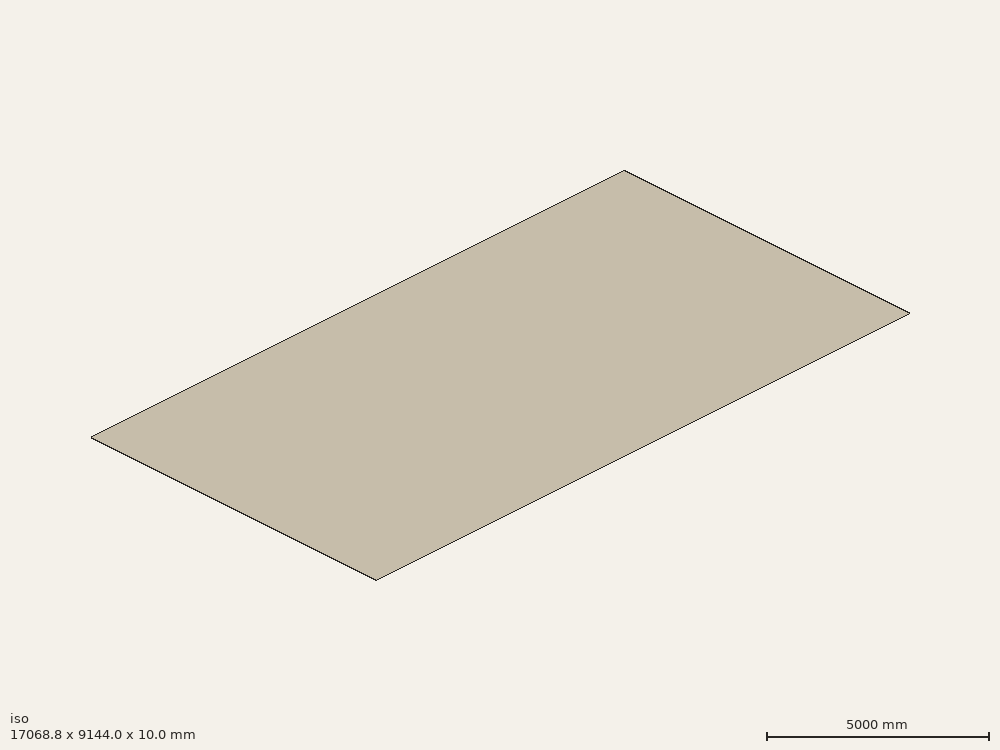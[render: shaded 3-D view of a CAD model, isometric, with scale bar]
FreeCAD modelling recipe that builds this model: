
FCSTD DOCUMENT  (FreeCAD 0.20R29177 (Git))
Label: grass
License: All rights reserved
LicenseURL: http://en.wikipedia.org/wiki/All_rights_reserved
objects: Sketcher::SketchObject×1, PartDesign::Pad×1, PartDesign::Body×1
note: 4 computed .brp shape members not serialized (recipe doc carries the construction recipe); baked Part::Feature solids carry a one-line shape summary decoded from their .brp

FEATURE [Sketcher::SketchObject] Sketch
  FullyConstrained = true
  MapMode = 5
  Support = -> [XY_Plane]
  expr: Constraints[10] = 30 * 12 * 25.4
  expr: Constraints[9] = 56 * 12 * 25.4
  sketch-geometry (4):
    g0: LineSegment StartX=0 StartY=0 StartZ=0 EndX=-17068.8 EndY=0 EndZ=0
    g1: LineSegment StartX=-17068.8 StartY=0 StartZ=0 EndX=-17068.8 EndY=-9144 EndZ=0
    g2: LineSegment StartX=-17068.8 StartY=-9144 StartZ=0 EndX=0 EndY=-9144 EndZ=0
    g3: LineSegment StartX=0 StartY=-9144 StartZ=0 EndX=0 EndY=0 EndZ=0
  constraints (11):
    c: Coincident(g0,g1)
    c: Coincident(g1,g2)
    c: Coincident(g2,g3)
    c: Coincident(g3,g0)
    c: Horizontal(g0)
    c: Horizontal(g2)
    c: Vertical(g1)
    c: Vertical(g3)
    c: Coincident(g0,g-1)
    c: DistanceX(g0,g0) = 17068.8
    c: DistanceY(g3,g3) = 9144
FEATURE [PartDesign::Pad] Pad
  Direction = (0,0,1)
  Length = 10
  Length2 = 10
  Profile = -> Sketch
  ReferenceAxis = -> Sketch [N_Axis]
  Type = 0
  expr: Length = 10mm
FEATURE [PartDesign::Body] Body
  Group = -> [Sketch,Pad]
  Origin = -> Origin
  Tip = -> Pad
